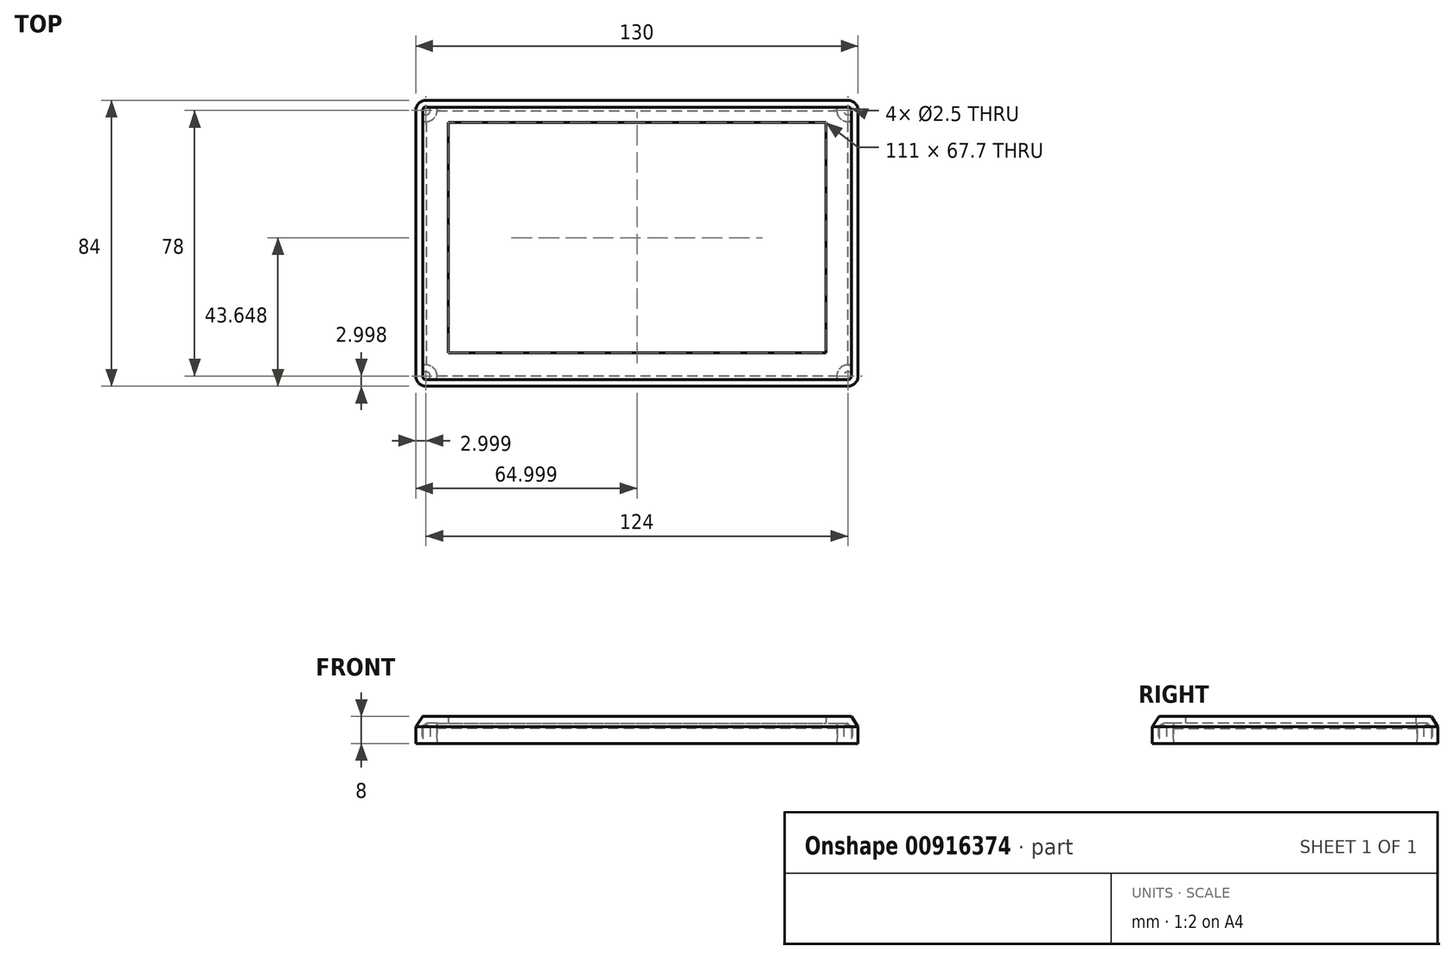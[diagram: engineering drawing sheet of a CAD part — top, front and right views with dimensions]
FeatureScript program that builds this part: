
annotation { "Feature Type Name" : "Feature", "Feature Type Description" : "" }
export const myFeature = defineFeature(function(context is Context, id is Id, definition is map)
    precondition{}
    {
        {
            var Q0;
            Q0=qCreatedBy(makeId("Top.planeOp"),FACE);
            var sketch = newSketch(context, id + "F0", { "sketchPlane" : qUnion([Q0])});
            skLineSegment(sketch, "E0.bottom", {"start": v(-59.52, 29.29) * mm, "end": v(64.48, 29.29) * mm});
            skLineSegment(sketch, "E0.top", {"start": v(-59.52, -54.71) * mm, "end": v(64.48, -54.71) * mm});
            skLineSegment(sketch, "E0.left", {"start": v(-62.52, 26.29) * mm, "end": v(-62.52, -51.71) * mm});
            skLineSegment(sketch, "E0.right", {"start": v(67.48, 26.29) * mm, "end": v(67.48, -51.71) * mm});
            skLineSegment(sketch, "E1.bottom", {"start": v(-53.02, 22.79) * mm, "end": v(57.98, 22.79) * mm});
            skLineSegment(sketch, "E1.top", {"start": v(-53.02, -44.91) * mm, "end": v(57.98, -44.91) * mm});
            skLineSegment(sketch, "E1.left", {"start": v(-53.02, 22.79) * mm, "end": v(-53.02, -44.91) * mm});
            skLineSegment(sketch, "E1.right", {"start": v(57.98, 22.79) * mm, "end": v(57.98, -44.91) * mm});
            skPoint(sketch, "E2.visualSharp", {"position": v(-62.52, 29.29) * mm});
            skArc(sketch, "E2.filletArc", {"start": v(-59.52, 29.29) * mm, "mid": v(-61.64, 28.4) * mm, "end": v(-62.52, 26.29) * mm});
            skPoint(sketch, "E3.visualSharp", {"position": v(67.48, 29.29) * mm});
            skArc(sketch, "E3.filletArc", {"start": v(67.48, 26.29) * mm, "mid": v(66.6, 28.4) * mm, "end": v(64.48, 29.29) * mm});
            skPoint(sketch, "E4.visualSharp", {"position": v(67.48, -54.71) * mm});
            skArc(sketch, "E4.filletArc", {"start": v(64.48, -54.71) * mm, "mid": v(66.6, -53.83) * mm, "end": v(67.48, -51.71) * mm});
            skPoint(sketch, "E5.visualSharp", {"position": v(-62.52, -54.71) * mm});
            skArc(sketch, "E5.filletArc", {"start": v(-62.52, -51.71) * mm, "mid": v(-61.64, -53.83) * mm, "end": v(-59.52, -54.71) * mm});
            skSolve(sketch);
        }
        {
            var Q0;
            Q0=makeQuery(id+"F0.imprint","IMPRINT",FACE,{"disambiguationData":[TD([[makeQuery(id+"F0.imprint","IMPRINT",EDGE,{"derivedFrom":sQuery(id+"F0.wireOp",EDGE,"E0.bottom")}),-1.0]])]});
            extrude(context, id + "F1", {"entities" : qUnion([Q0]), "depth" : 8 * mm, "offsetDistance" : 25 * mm});
        }
        {
            var Q0;
            Q0=makeQuery(id+"F1.opExtrude","CAP_EDGE",EDGE,{"disambiguationData":[OSD([sQuery(id+"F0.wireOp",EDGE,"E0.top")])],"isStart":false});
            chamfer(context, id + "F2", {"entities" : qUnion([Q0]), "chamferType" : ChamferType.TWO_OFFSETS, "width1" : 2 * mm, "oppositeDirection" : false, "width2" : 3 * mm, "tangentPropagation" : true});
        }
        {
            var Q0;
            Q0=makeQuery(id+"F1.opExtrude","CAP_FACE",FACE,{"disambiguationData":[OSD([sQuery(id+"F0.wireOp",EDGE,"E0.bottom"),sQuery(id+"F0.wireOp",EDGE,"E0.top"),sQuery(id+"F0.wireOp",EDGE,"E0.left"),sQuery(id+"F0.wireOp",EDGE,"E0.right"),sQuery(id+"F0.wireOp",EDGE,"E1.bottom"),sQuery(id+"F0.wireOp",EDGE,"E1.top"),sQuery(id+"F0.wireOp",EDGE,"E1.left"),sQuery(id+"F0.wireOp",EDGE,"E1.right"),sQuery(id+"F0.wireOp",EDGE,"E2.filletArc"),sQuery(id+"F0.wireOp",EDGE,"E3.filletArc"),sQuery(id+"F0.wireOp",EDGE,"E4.filletArc"),sQuery(id+"F0.wireOp",EDGE,"E5.filletArc")])],"isStart":true});
            var sketch = newSketch(context, id + "F3", { "sketchPlane" : qUnion([Q0])});
            skPoint(sketch, "E6", {"position": v(-59.52, -26.29) * mm});
            skPoint(sketch, "E7", {"position": v(-59.52, 51.71) * mm});
            skPoint(sketch, "E8", {"position": v(64.48, 51.71) * mm});
            skPoint(sketch, "E9", {"position": v(64.48, -26.29) * mm});
            skSolve(sketch);
        }
        {
            var Q0;
            Q0=sQuery(id+"F3.wireOp",VERTEX,"E6");
            var Q1;
            Q1=sQuery(id+"F3.wireOp",VERTEX,"E7");
            var Q2;
            Q2=sQuery(id+"F3.wireOp",VERTEX,"E8");
            var Q3;
            Q3=sQuery(id+"F3.wireOp",VERTEX,"E9");
            var Q4;
            Q4=makeQuery(id+"F1.opExtrude","SWEPT_BODY",BODY,{"disambiguationData":[OSD([sQuery(id+"F0.wireOp",EDGE,"E0.bottom"),sQuery(id+"F0.wireOp",EDGE,"E0.top"),sQuery(id+"F0.wireOp",EDGE,"E0.left"),sQuery(id+"F0.wireOp",EDGE,"E0.right"),sQuery(id+"F0.wireOp",EDGE,"E1.bottom"),sQuery(id+"F0.wireOp",EDGE,"E1.top"),sQuery(id+"F0.wireOp",EDGE,"E1.left"),sQuery(id+"F0.wireOp",EDGE,"E1.right"),sQuery(id+"F0.wireOp",EDGE,"E2.filletArc"),sQuery(id+"F0.wireOp",EDGE,"E3.filletArc"),sQuery(id+"F0.wireOp",EDGE,"E4.filletArc"),sQuery(id+"F0.wireOp",EDGE,"E5.filletArc")])]});
            hole(context, id + "F4", {"style" : HoleStyle.SIMPLE, "endStyle" : HoleEndStyle.BLIND, "standardTappedOrClearance" : lookupTablePath({ "standard" : "ISO", "engagement" : "75%", "pitch" : "0.5 mm", "size" : "M3", "type" : "Tapped" }), "standardBlindInLast" : lookupTablePath({ "standard" : "ISO", "engagement" : "75%", "pitch" : "0.5 mm", "size" : "M3", "type" : "Tapped" }), "holeDiameter" : 2.5 * mm, "majorDiameter" : 3 * mm, "showTappedDepth" : true, "holeDepth" : 5 * mm, "tappedDepth" : 4.5 * mm, "tapClearance" : 1, "locations" : qUnion([Q0, Q1, Q2, Q3]), "scope" : qUnion([Q4])});
        }
        {
            var Q0;
            Q0=makeQuery(id+"F1.opExtrude","CAP_FACE",FACE,{"disambiguationData":[OSD([sQuery(id+"F0.wireOp",EDGE,"E0.bottom"),sQuery(id+"F0.wireOp",EDGE,"E0.top"),sQuery(id+"F0.wireOp",EDGE,"E0.left"),sQuery(id+"F0.wireOp",EDGE,"E0.right"),sQuery(id+"F0.wireOp",EDGE,"E1.bottom"),sQuery(id+"F0.wireOp",EDGE,"E1.top"),sQuery(id+"F0.wireOp",EDGE,"E1.left"),sQuery(id+"F0.wireOp",EDGE,"E1.right"),sQuery(id+"F0.wireOp",EDGE,"E2.filletArc"),sQuery(id+"F0.wireOp",EDGE,"E3.filletArc"),sQuery(id+"F0.wireOp",EDGE,"E4.filletArc"),sQuery(id+"F0.wireOp",EDGE,"E5.filletArc")])],"isStart":true});
            var Q1;
            Q1=makeQuery(id+"F1.opExtrude","SWEPT_FACE",FACE,{"disambiguationData":[OSD([sQuery(id+"F0.wireOp",EDGE,"E1.right")])]});
            var Q2;
            Q2=makeQuery(id+"F1.opExtrude","SWEPT_FACE",FACE,{"disambiguationData":[OSD([sQuery(id+"F0.wireOp",EDGE,"E1.bottom")])]});
            var Q3;
            Q3=makeQuery(id+"F1.opExtrude","SWEPT_FACE",FACE,{"disambiguationData":[OSD([sQuery(id+"F0.wireOp",EDGE,"E1.left")])]});
            var Q4;
            Q4=makeQuery(id+"F1.opExtrude","SWEPT_FACE",FACE,{"disambiguationData":[OSD([sQuery(id+"F0.wireOp",EDGE,"E1.top")])]});
            shell(context, id + "F5", {"entities" : qUnion([Q0, Q1, Q2, Q3, Q4]), "thickness" : 2 * mm});
        }
    });
